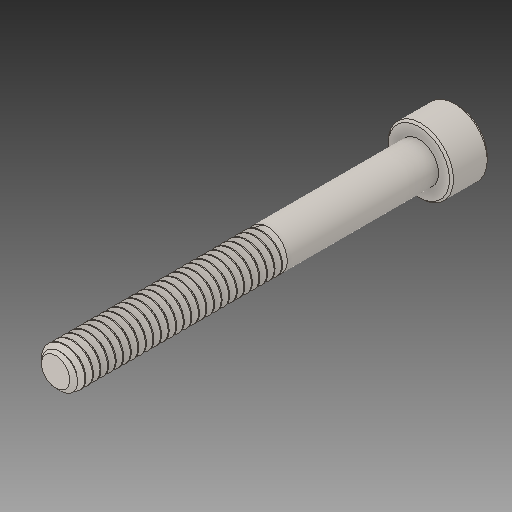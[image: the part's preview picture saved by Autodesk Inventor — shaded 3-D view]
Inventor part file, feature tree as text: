
AUTODESK INVENTOR PART (.ipt)
format: ipt  version: 2017 (Build 210142000, 142)  size: 900,608 bytes
history: native  units: in
note: dims shown in document units (in); Inventor stores cm internally (conversion verified against a paired STEP export)
features: chamfer x1
ambient origin geometry x8: Origin, YZ Plane, XZ Plane, XY Plane, X Axis, Y Axis, Z Axis, Center Point
bodies: Solid1 (feature_tree)
feature tree (1):
  chamfer  "Chamfer2"  [1 undecoded]
note: 1 required parameter value undecoded (feature->parameter linkage not recoverable at this tier; creation-order binding heuristic only, values carry confidence <= 0.55)
